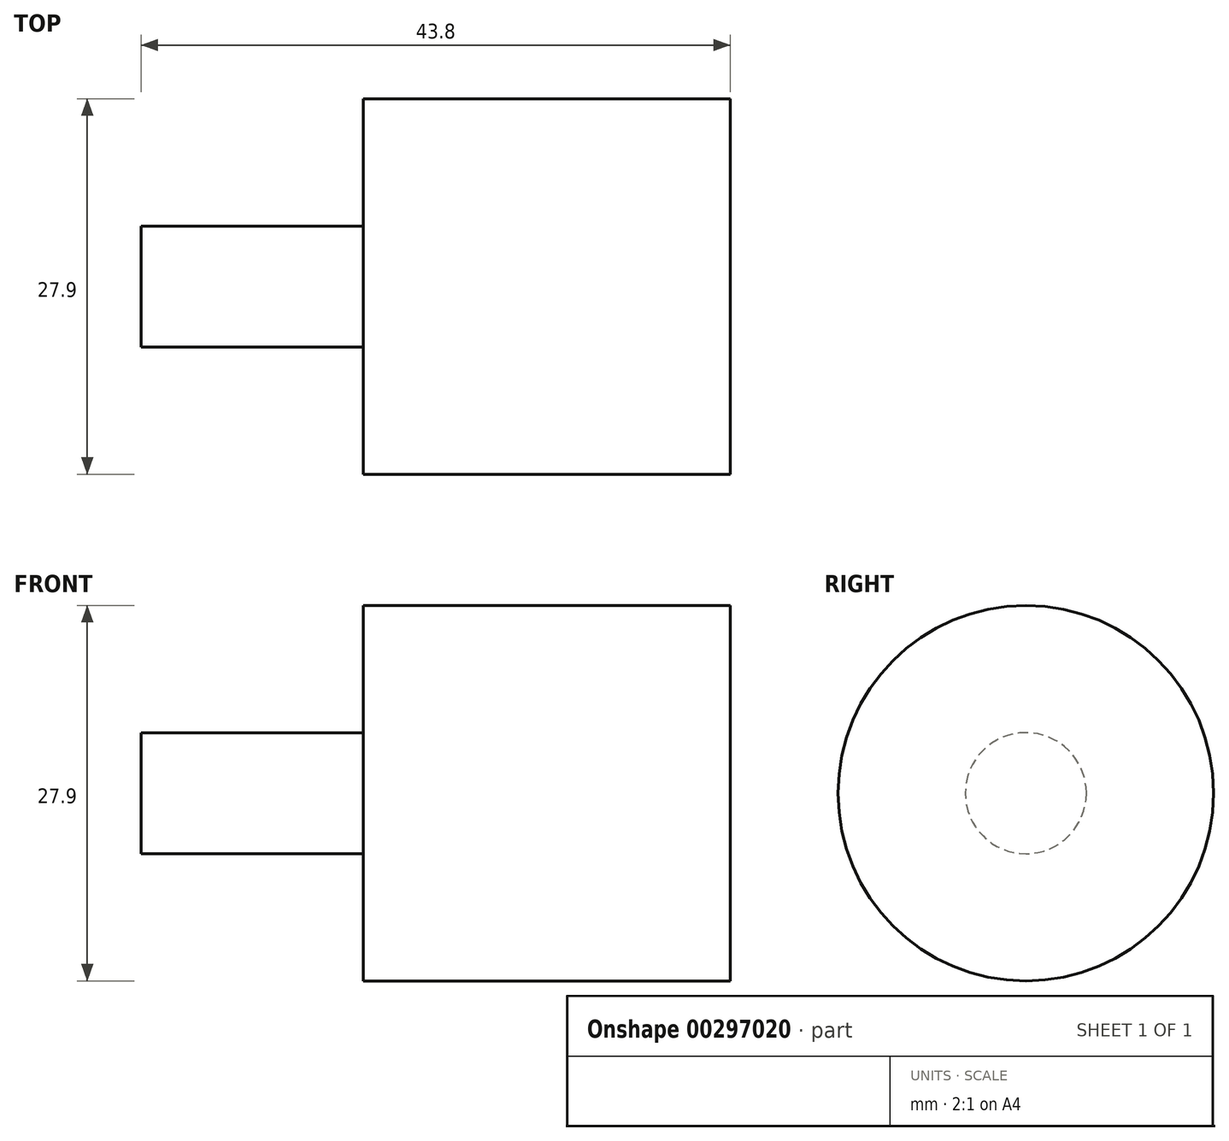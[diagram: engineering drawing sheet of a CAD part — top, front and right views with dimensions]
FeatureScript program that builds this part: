
annotation { "Feature Type Name" : "Feature", "Feature Type Description" : "" }
export const myFeature = defineFeature(function(context is Context, id is Id, definition is map)
    precondition{}
    {
        {
            var Q0;
            Q0=qCreatedBy(makeId("Front.planeOp"),FACE);
            var sketch = newSketch(context, id + "F0", { "sketchPlane" : qUnion([Q0])});
            skLineSegment(sketch, "E0.bottom", {"start": v(-27.3, 13.95) * mm, "end": v(0, 13.95) * mm});
            skLineSegment(sketch, "E0.top", {"start": v(-27.3, -13.95) * mm, "end": v(0, -13.95) * mm});
            skLineSegment(sketch, "E0.left", {"start": v(-27.3, 13.95) * mm, "end": v(-27.3, -13.95) * mm});
            skLineSegment(sketch, "E0.right", {"start": v(0, 13.95) * mm, "end": v(0, -13.95) * mm});
            skLineSegment(sketch, "E1.bottom", {"start": v(-43.8, -4.5) * mm, "end": v(-27.3, -4.5) * mm});
            skLineSegment(sketch, "E1.top", {"start": v(-43.8, 4.5) * mm, "end": v(-27.3, 4.5) * mm});
            skLineSegment(sketch, "E1.left", {"start": v(-43.8, 4.5) * mm, "end": v(-43.8, -4.5) * mm});
            skLineSegment(sketch, "E1.right", {"start": v(-27.3, 4.5) * mm, "end": v(-27.3, -4.5) * mm});
            skLineSegment(sketch, "E2", {"start": v(0, 0) * mm, "end": v(-43.8, 0) * mm});
            skSolve(sketch);
        }
        {
            var Q0;
            {var subQ1=sQuery(id+"F0.wireOp",EDGE,"E0.bottom");Q0=makeQuery(id+"F0.imprint","IMPRINT",FACE,{"disambiguationData":[TD([[makeQuery(id+"F0.imprint","IMPRINT",EDGE,{"derivedFrom":subQ1}),-1.0]])]});}
            var Q1;
            {var subQ0=sQuery(id+"F0.wireOp",EDGE,"E1.top");Q1=makeQuery(id+"F0.imprint","IMPRINT",FACE,{"disambiguationData":[TD([[makeQuery(id+"F0.imprint","IMPRINT",EDGE,{"derivedFrom":subQ0}),-1.0]])]});}
            var Q2;
            Q2=sQuery(id+"F0.wireOp",EDGE,"E2");
            revolve(context, id + "F1", {"entities" : qUnion([Q0, Q1]), "axis" : qUnion([Q2]), "revolveType" : RevolveType.FULL});
        }
    });
